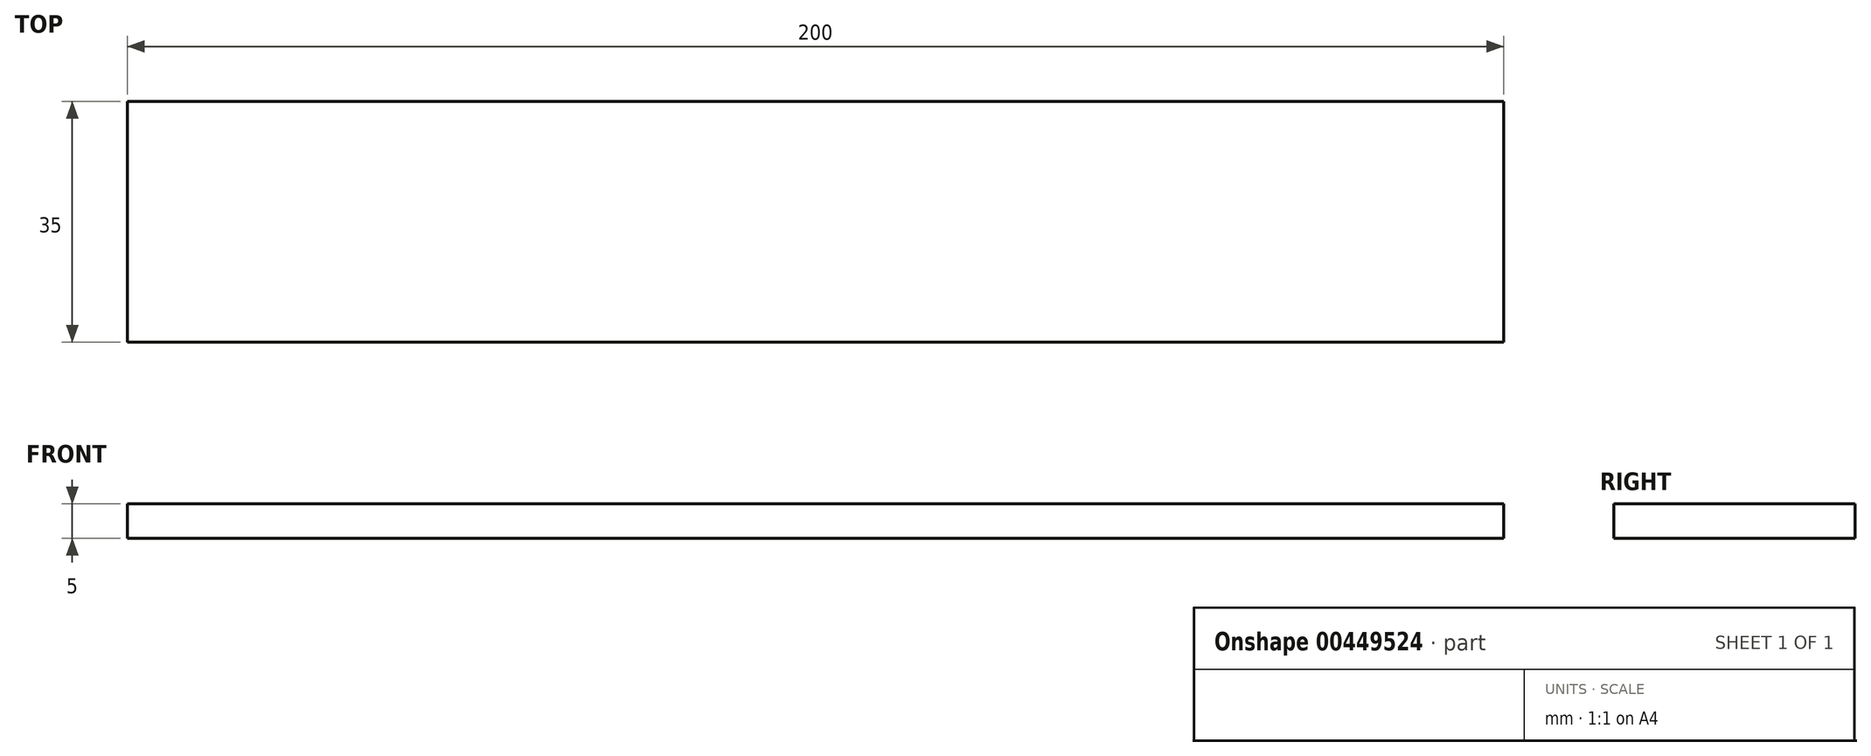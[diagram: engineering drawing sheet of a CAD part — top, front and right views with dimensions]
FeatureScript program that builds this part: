
annotation { "Feature Type Name" : "Feature", "Feature Type Description" : "" }
export const myFeature = defineFeature(function(context is Context, id is Id, definition is map)
    precondition{}
    {
        {
            var Q0;
            Q0=qCreatedBy(makeId("Top.planeOp"),FACE);
            var sketch = newSketch(context, id + "F0", { "sketchPlane" : qUnion([Q0])});
            skLineSegment(sketch, "E0.bottom", {"start": v(0, 35) * mm, "end": v(200, 35) * mm});
            skLineSegment(sketch, "E0.top", {"start": v(0, 0) * mm, "end": v(200, 0) * mm});
            skLineSegment(sketch, "E0.left", {"start": v(0, 35) * mm, "end": v(0, 0) * mm});
            skLineSegment(sketch, "E0.right", {"start": v(200, 35) * mm, "end": v(200, 0) * mm});
            skSolve(sketch);
        }
        {
            var Q0;
            Q0=makeQuery(id+"F0.imprint","IMPRINT",FACE,{"disambiguationData":[TD([[makeQuery(id+"F0.imprint","IMPRINT",EDGE,{"derivedFrom":sQuery(id+"F0.wireOp",EDGE,"E0.bottom")}),-1.0]])]});
            extrude(context, id + "F1", {"entities" : qUnion([Q0]), "depth" : 5 * mm});
        }
    });
